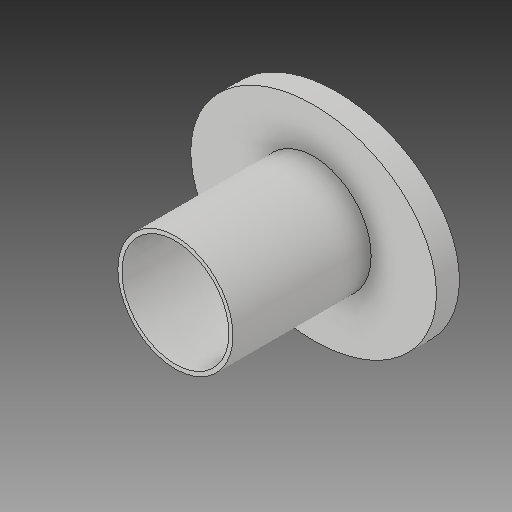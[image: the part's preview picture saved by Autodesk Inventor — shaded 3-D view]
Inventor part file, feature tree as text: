
AUTODESK INVENTOR PART (.ipt)
format: ipt  version: 2017 (Build 210142000, 142)  size: 120,832 bytes
history: native  units: mm
features: sketch x4, other x3
ambient origin geometry x8: Origin, YZ Plane, XZ Plane, XY Plane, X Axis, Y Axis, Z Axis, Center Point
bodies: Solid1 (feature_tree)
feature tree (7):
  other  "Pushfit-adapter-cap.ipt"
  other  "Solid1::Pushfit-adapter-cap.ipt"
  other  "TaggingFeature1"
  sketch  "Sketch1"  dims[d0=10.0mm]
  sketch  "Sketch2"
  sketch  "Sketch3"
  sketch  "Sketch4"
